# Revit family: Malvestio_Cubik_334550___
name_source: partatom
category: Furniture
revit_build: Autodesk Revit 2018 (Build: 20190510_1515(x64)
units: mm (PartAtom-declared; Revit-internal decimal feet)

## family parameters
Always vertical = Yes
Cut with Voids When Loaded = No
OmniClass Number = 23.40.20.17.14.11
OmniClass Title = Beds
Room Calculation Point = No
Shared = No
Work Plane-Based = No

## types (1)
- 334550
    DIM_Depth = 410 mm  [stored 1.34514 ft]
    DIM_Height = 665 mm  [stored 2.18176 ft]
    DIM_Width = 540 mm  [stored 1.77165 ft]
    Keynote = 0
    Manufacturer = Malvestio Spa
    Mat_Case = RAL 9010
    Mat_Towel_Holder = Plastic-Dark Gray
    Mat_Weel_Tyre = Rubber Black
    Model = 334550
    Product Code = 334550
    Product Disclaimer = Malvestio Spa declines any responsibility for
the modifications of the type parameters.
The company is not responsible for the
objects/drawings and the correct
production/installation.
The company reserves the right to make technical
improvements or modifications of any type without
prior notice to the customer.
All rights reserved.
    Product Model = 334550
    Product Series = Cubik
    Product URL = https://www.malvestio.com
    URL = https://www.malvestio.com
    Weight = 13.00 kg

note: [stored X ft] marks values corroborated as IEEE doubles in the binary element streams (Revit-internal decimal feet)

## geometry (parser evidence)
native form markers: Sweep x9
no freeform markers — native parametric forms only
